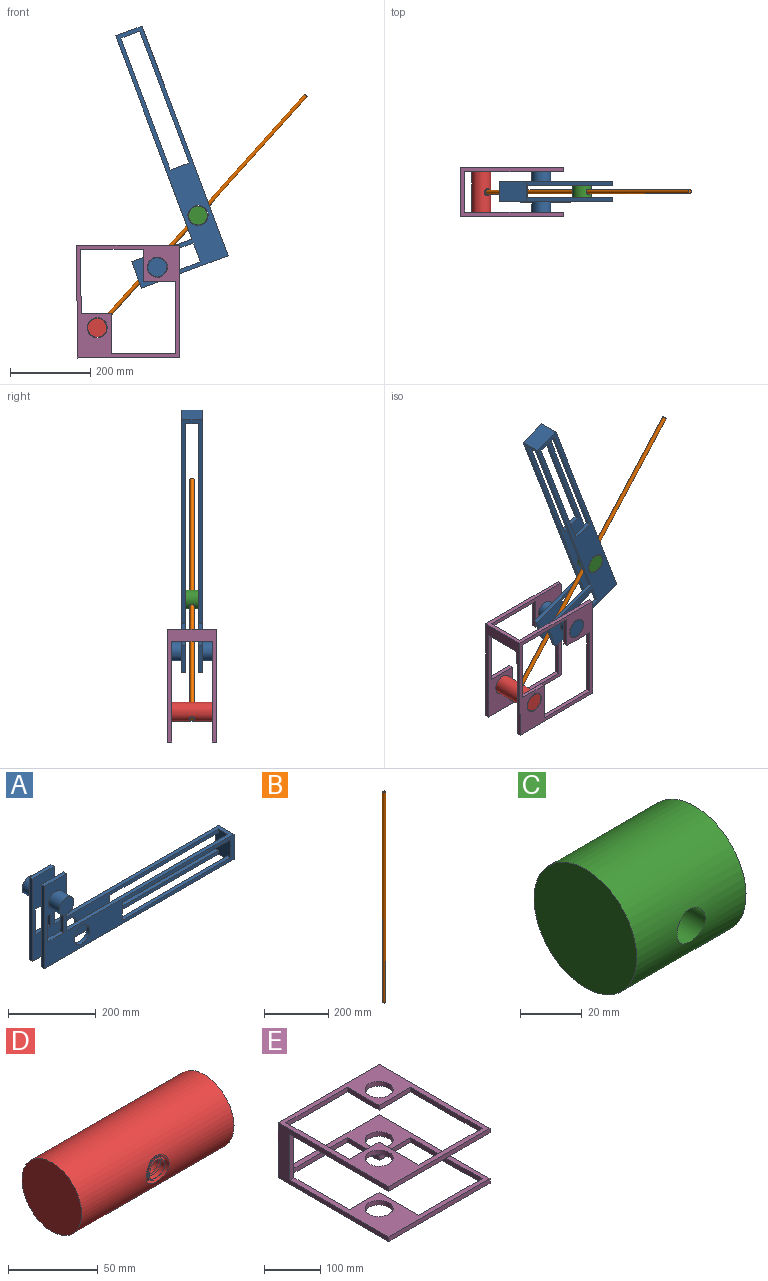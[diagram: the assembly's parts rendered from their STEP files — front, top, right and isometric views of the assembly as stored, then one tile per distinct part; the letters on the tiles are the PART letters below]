
ASSEMBLY  parts=5 mates=5
PART A: 34 faces, bbox 610x120x230 mm
  f0: plane 610x230mm, normal (0,-1,0), area 29126.6mm2, adj f4,f7,f9,f10,f11,f12,f13,f17
  f1: plane 610x230mm, normal (0,1,0), area 29126.6mm2, adj f5,f6,f7,f8,f9,f10,f15,f17
  f2: plane 600x230mm, normal (0,-1,0), area 30161.5mm2, adj f5,f6,f7,f8,f9,f17,f25,f26
  f3: plane 600x230mm, normal (0,1,0), area 30161.5mm2, adj f4,f7,f9,f11,f12,f17,f18,f19
  f4: plane 230x10mm, normal (-1,0,0), area 2300mm2, adj f0,f3,f9,f12
  f5: plane 70x10mm, normal (0,0,1), area 700mm2, adj f1,f2,f6,f8
  f6: plane 230x10mm, normal (-1,0,0), area 2300mm2, adj f1,f2,f5,f9
  f7: plane 540x50mm, normal (0,0,1), area 11100mm2, adj f0,f1,f2,f3,f8,f10,f11,f17
  f8: plane 160x10mm, normal (1,0,0), area 1600mm2, adj f1,f2,f5,f7
  f9: plane 610x50mm, normal (0,0,-1), area 12500mm2, adj f0,f1,f2,f3,f4,f6,f10,f17
  f10: plane 70x50mm, normal (1,0,0), area 3500mm2, adj f0,f1,f7,f9
  f11: plane 160x10mm, normal (1,0,0), area 1600mm2, adj f0,f3,f7,f12
  f12: plane 70x10mm, normal (0,0,1), area 700mm2, adj f0,f3,f4,f11
  f13: cylinder r=23.5mm len=47mm, axis (0,1,0), area 5167.9mm2, adj f0,f14
  f14: plane 47x47mm, normal (0,-1,0), area 1734.9mm2, adj f13
  f15: cylinder r=23.5mm len=47mm, axis (0,-1,0), area 5167.9mm2, adj f1,f16
  f16: plane 47x47mm, normal (0,1,0), area 1734.9mm2, adj f15
  f17: plane 70x50mm, normal (-1,0,0), area 3100mm2, adj f0,f1,f2,f3,f7,f9,f22,f24
  f18: plane 50x10mm, normal (0,0,-1), area 500mm2, adj f0,f3,f19,f21
  f19: plane 71.5x10mm, normal (-1,0,0), area 715mm2, adj f0,f3,f18,f20
  f20: plane 50x10mm, normal (0,0,1), area 500mm2, adj f0,f3,f19,f21
  f21: plane 71.5x10mm, normal (1,0,0), area 715mm2, adj f0,f3,f18,f20
  f22: plane 350x10mm, normal (0,0,1), area 3500mm2, adj f0,f3,f17,f23
  f23: plane 50x10mm, normal (1,0,0), area 500mm2, adj f0,f3,f22,f24
  f24: plane 350x10mm, normal (0,0,-1), area 3500mm2, adj f0,f3,f17,f23
  f25: plane 71.5x10mm, normal (1,0,0), area 715mm2, adj f1,f2,f26,f28
  f26: plane 50x10mm, normal (0,0,1), area 500mm2, adj f1,f2,f25,f27
  f27: plane 71.5x10mm, normal (-1,0,0), area 715mm2, adj f1,f2,f26,f28
  f28: plane 50x10mm, normal (0,0,-1), area 500mm2, adj f1,f2,f25,f27
  f29: plane 350x10mm, normal (0,0,-1), area 3500mm2, adj f1,f2,f17,f30
  f30: plane 50x10mm, normal (1,0,0), area 500mm2, adj f1,f2,f29,f31
  f31: plane 350x10mm, normal (0,0,1), area 3500mm2, adj f1,f2,f17,f30
  f32: cylinder r=25mm len=50mm, axis (0,-1,0), area 1570.8mm2, adj f0,f3
  f33: cylinder r=25mm len=50mm, axis (0,-1,0), area 1570.8mm2, adj f1,f2
PART B: 3 faces, bbox 10x10x800 mm
  f0: cylinder r=5mm len=800mm, axis (0,0,-1), area 25132.7mm2, adj f1,f2
  f1: plane 10x10mm, normal (0,0,1), area 78.5mm2, adj f0
  f2: plane 10x10mm, normal (0,0,-1), area 78.5mm2, adj f0
PART C: 4 faces, bbox 50x47x47 mm
  f0: cylinder r=23.5mm len=50mm, axis (1,0,0), area 7114.4mm2, adj f1,f2,f3
  f1: plane 47x47mm, normal (-1,0,0), area 1734.9mm2, adj f0
  f2: cylinder r=6.5mm len=47mm, axis (0,1,0), area 1882.3mm2, adj f0
  f3: plane 47x47mm, normal (1,0,0), area 1734.9mm2, adj f0
PART D: 18 faces, bbox 120x48.7x47 mm
  f0: cylinder r=23.5mm len=120mm, axis (-1,0,0), area 17326.1mm2, adj f1,f11,f12,f13
  f1: cylinder r=6.5mm len=13mm, axis (0,1,0), area 373.7mm2, adj f0,f2,f14,f15,f16
  f2: cylinder r=6.5mm len=13mm, axis (0,1,0), area 132.8mm2, adj f1,f3,f15,f16
  f3: cylinder r=6.5mm len=13mm, axis (0,1,0), area 132.8mm2, adj f2,f4,f15,f16
  f4: cylinder r=6.5mm len=13mm, axis (0,1,0), area 132.8mm2, adj f3,f5,f15,f16
  f5: cylinder r=6.5mm len=13mm, axis (0,1,0), area 132.8mm2, adj f4,f6,f15,f16
  f6: cylinder r=6.5mm len=13mm, axis (0,1,0), area 132.8mm2, adj f5,f7,f15,f16
  f7: cylinder r=6.5mm len=13mm, axis (0,1,0), area 132.8mm2, adj f6,f8,f15,f16
  f8: cylinder r=6.5mm len=13mm, axis (0,1,0), area 129.1mm2, adj f7,f9,f10,f15,f16
  f9: cylinder r=6.5mm len=12.36mm, axis (0,1,0), area 17.2mm2, adj f8,f10,f16
  f10: cylinder r=23.5mm len=13.46mm, axis (-1,0,0), area 23.3mm2, adj f8,f9,f15,f16
  f11: plane 47x47mm, normal (1,0,0), area 1734.9mm2, adj f0
  f12: plane 47x47mm, normal (-1,0,0), area 1734.9mm2, adj f0
  f13: cylinder r=8.98mm len=41.22mm, axis (0,1,0), area 2185.7mm2, adj f0,f14,f17
  f14: plane 6.01x3.66mm, normal (0.6,0,0.8), area 18.2mm2, adj f1,f13,f15,f16,f17
  f15: bspline ~42.41x15.26mm, area 691mm2, adj f1,f2,f3,f4,f5,f6,f7,f8
  f16: bspline ~41.67x17.79mm, area 766.8mm2, adj f1,f2,f3,f4,f5,f6,f7,f8
  f17: bspline ~20.58x19.11mm, area 77mm2, adj f13,f14,f15
PART E: 32 faces, bbox 255x280x120 mm
  f0: plane 255x10mm, normal (0,-1,0), area 2550mm2, adj f1,f3,f6,f9
  f1: plane 280x10mm, normal (1,0,0), area 2800mm2, adj f0,f2,f6,f9
  f2: plane 255x120mm, normal (0,1,0), area 6080mm2, adj f1,f3,f5,f6,f7,f8,f9,f10
  f3: plane 280x120mm, normal (-1,0,0), area 8600mm2, adj f0,f2,f4,f6,f7,f8,f9,f15
  f4: plane 255x10mm, normal (0,-1,0), area 2550mm2, adj f3,f5,f7,f8
  f5: plane 280x10mm, normal (1,0,0), area 2800mm2, adj f2,f4,f7,f8
  f6: plane 280x255mm, normal (0,0,1), area 20273mm2, adj f0,f1,f2,f3,f11,f12,f16,f17
  f7: plane 280x255mm, normal (0,0,-1), area 20273mm2, adj f2,f3,f4,f5,f13,f14,f24,f25
  f8: plane 280x255mm, normal (0,0,1), area 19979mm2, adj f2,f3,f4,f5,f10,f13,f14,f15
  f9: plane 280x255mm, normal (0,0,-1), area 19979mm2, adj f0,f1,f2,f3,f10,f11,f12,f15
  f10: plane 100x30mm, normal (1,0,0), area 3000mm2, adj f2,f8,f9,f15
  f11: cylinder r=25mm len=50mm, axis (0,0,1), area 1570.8mm2, adj f6,f9
  f12: cylinder r=25mm len=50mm, axis (0,0,1), area 1570.8mm2, adj f6,f9
  f13: cylinder r=25mm len=50mm, axis (0,0,1), area 1570.8mm2, adj f7,f8
  f14: cylinder r=25mm len=50mm, axis (0,0,1), area 1570.8mm2, adj f7,f8
  f15: plane 100x9.8mm, normal (0,-1,0), area 980mm2, adj f3,f8,f9,f10
  f16: plane 155x10mm, normal (0,-1,0), area 1550mm2, adj f6,f9,f17,f23
  f17: plane 80x10mm, normal (-1,0,0), area 800mm2, adj f6,f9,f16,f18
  f18: plane 80x10mm, normal (0,-1,0), area 800mm2, adj f6,f9,f17,f19
  f19: plane 180x10mm, normal (-1,0,0), area 1800mm2, adj f6,f9,f18,f20
  f20: plane 160x10mm, normal (0,1,0), area 1600mm2, adj f6,f9,f19,f21
  f21: plane 100x10mm, normal (1,0,0), area 1000mm2, adj f6,f9,f20,f22
  f22: plane 75x10mm, normal (0,1,0), area 750mm2, adj f6,f9,f21,f23
  f23: plane 160x10mm, normal (1,0,0), area 1600mm2, adj f6,f9,f16,f22
  f24: plane 160x10mm, normal (1,0,0), area 1600mm2, adj f7,f8,f25,f31
  f25: plane 75x10mm, normal (0,1,0), area 750mm2, adj f7,f8,f24,f26
  f26: plane 100x10mm, normal (1,0,0), area 1000mm2, adj f7,f8,f25,f27
  f27: plane 160x10mm, normal (0,1,0), area 1600mm2, adj f7,f8,f26,f28
  f28: plane 180x10mm, normal (-1,0,0), area 1800mm2, adj f7,f8,f27,f29
  f29: plane 80x10mm, normal (0,-1,0), area 800mm2, adj f7,f8,f28,f30
  f30: plane 80x10mm, normal (-1,0,0), area 800mm2, adj f7,f8,f29,f31
  f31: plane 155x10mm, normal (0,-1,0), area 1550mm2, adj f7,f8,f24,f30
PLACE A rot(axis=(0,-1,0),110.5deg) t=(326.63,270.61,192.91)mm
PLACE B rot(axis=(0,1,0),41.9deg) t=(-14.85,245.61,-4)mm
PLACE C rot(axis=(-0.38,-0.38,0.85),99.6deg) t=(196.2,220.61,141.29)mm
PLACE D rot(axis=(-0.38,-0.38,0.85),99.6deg) t=(-41.91,195.61,-108.99)mm
PLACE E rot(axis=(1,0,0),90deg) t=(-48.67,305.61,-61.48)mm fixed
MATE revolute C.f0 <-> A.f32  axis (0,-1,0) through (251.75,220.61,292.99)mm
MATE revolute D.f0 <-> E.f12  axis (0,-1,0) through (1.05,185.61,13.71)mm
MATE revolute A.f13 <-> E.f11  axis (0,1,0) through (150.48,185.61,164.27)mm
MATE slider B.f0 <-> C.f2  axis (-0.67,0,-0.74) through (252.35,245.61,293.67)mm
MATE revolute B.f0 <-> D.f1  axis (-0.67,0,-0.74) through (-14.85,245.61,-4)mm
